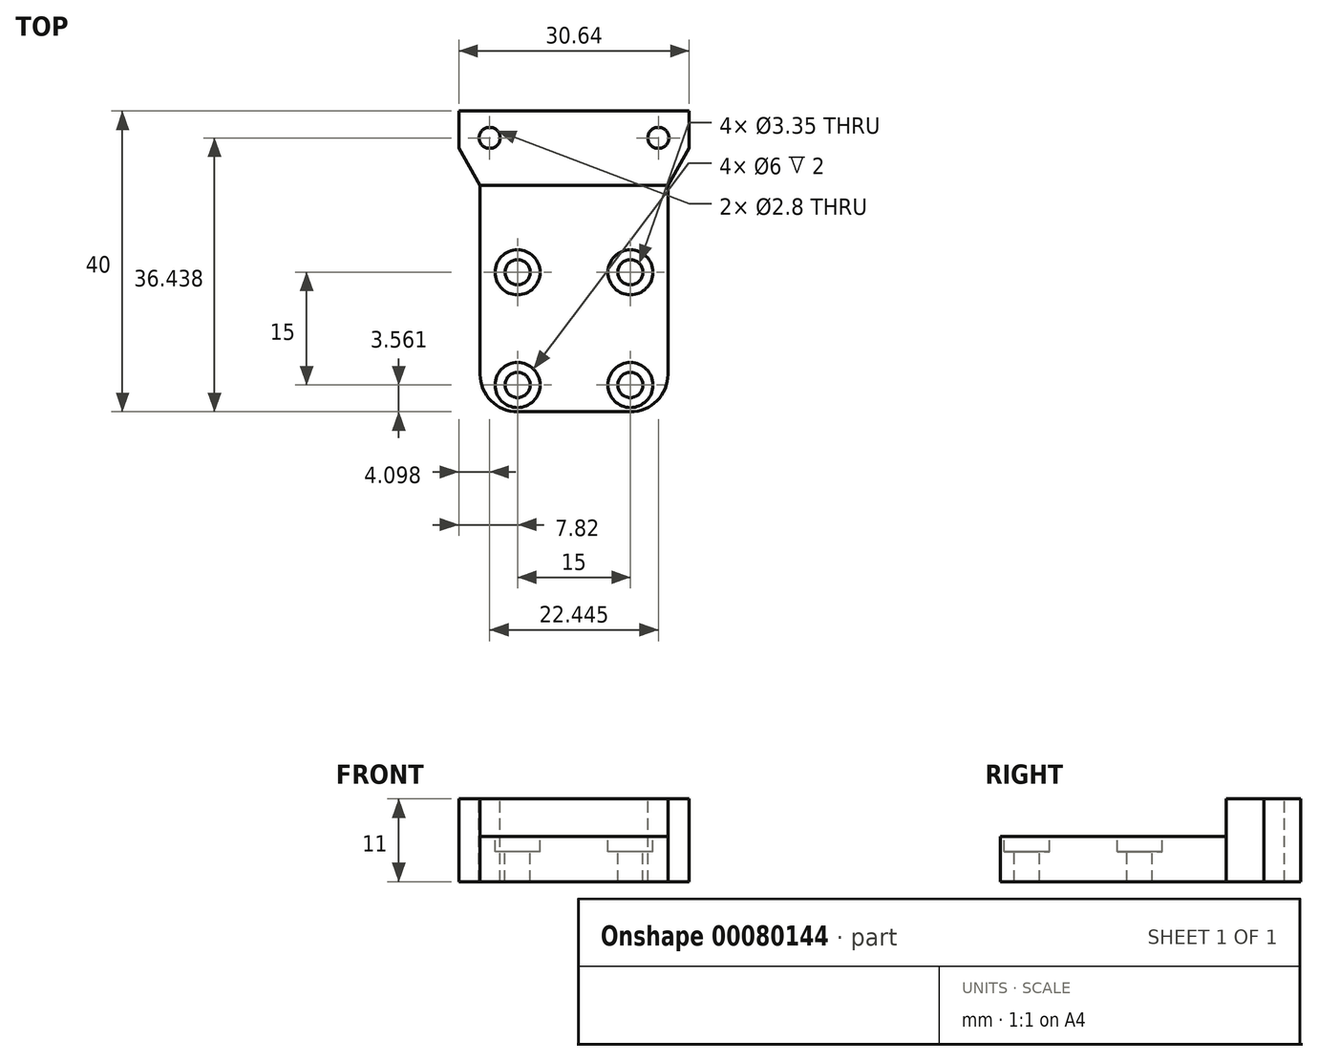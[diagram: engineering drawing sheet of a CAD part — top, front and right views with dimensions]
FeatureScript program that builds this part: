
annotation { "Feature Type Name" : "Feature", "Feature Type Description" : "" }
export const myFeature = defineFeature(function(context is Context, id is Id, definition is map)
    precondition{}
    {
        {
            var Q0;
            Q0=qCreatedBy(makeId("Top.planeOp"),FACE);
            var sketch = newSketch(context, id + "F0", { "sketchPlane" : qUnion([Q0])});
            skLineSegment(sketch, "E0.bottom", {"start": v(0, 0) * mm, "end": v(25, 0) * mm});
            skLineSegment(sketch, "E0.top", {"start": v(-2.82, 40) * mm, "end": v(27.82, 40) * mm});
            skLineSegment(sketch, "E1", {"start": v(0, 30.1) * mm, "end": v(25, 30.1) * mm});
            skLineSegment(sketch, "E2", {"start": v(-2.82, 35.1) * mm, "end": v(27.82, 35.1) * mm});
            skLineSegment(sketch, "E3", {"start": v(0, 0) * mm, "end": v(0, 30.1) * mm});
            skLineSegment(sketch, "E4", {"start": v(0, 30.1) * mm, "end": v(-2.82, 35.1) * mm});
            skLineSegment(sketch, "E5", {"start": v(-2.82, 35.1) * mm, "end": v(-2.82, 40) * mm});
            skLineSegment(sketch, "E6", {"start": v(25, 0) * mm, "end": v(25, 30.1) * mm});
            skLineSegment(sketch, "E7", {"start": v(25, 30.1) * mm, "end": v(27.82, 35.1) * mm});
            skLineSegment(sketch, "E8", {"start": v(27.82, 35.1) * mm, "end": v(27.82, 40) * mm});
            skSolve(sketch);
        }
        {
            var Q0;
            Q0=qSketchRegion(id+"F0",true);
            extrude(context, id + "F1", {"entities" : qUnion([Q0]), "depth" : 6 * mm});
        }
        {
            var Q0;
            Q0=makeQuery(id+"F1.opExtrude","CAP_FACE",FACE,{"disambiguationData":[OSD([sQuery(id+"F0.wireOp",EDGE,"E0.bottom"),sQuery(id+"F0.wireOp",EDGE,"E0.top"),sQuery(id+"F0.wireOp",EDGE,"E3"),sQuery(id+"F0.wireOp",EDGE,"E4"),sQuery(id+"F0.wireOp",EDGE,"E5"),sQuery(id+"F0.wireOp",EDGE,"E6"),sQuery(id+"F0.wireOp",EDGE,"E7"),sQuery(id+"F0.wireOp",EDGE,"E8")])],"isStart":false});
            var sketch = newSketch(context, id + "F2", { "sketchPlane" : qUnion([Q0])});
            skCircle(sketch, "E9", {"center": v(5, 18.56) * mm, "radius": 1.68 * mm});
            skCircle(sketch, "E10", {"center": v(20, 18.56) * mm, "radius": 1.68 * mm});
            skCircle(sketch, "E11", {"center": v(5, 3.56) * mm, "radius": 1.68 * mm});
            skCircle(sketch, "E12", {"center": v(20, 3.56) * mm, "radius": 1.68 * mm});
            skLineSegment(sketch, "E13", {"start": v(5, 18.56) * mm, "end": v(0, 18.56) * mm});
            skLineSegment(sketch, "E14", {"start": v(20, 3.56) * mm, "end": v(25, 3.56) * mm});
            skCircle(sketch, "E15", {"center": v(5, 18.56) * mm, "radius": 3 * mm});
            skCircle(sketch, "E16", {"center": v(20, 18.56) * mm, "radius": 3 * mm});
            skCircle(sketch, "E17", {"center": v(5, 3.56) * mm, "radius": 3 * mm});
            skCircle(sketch, "E18", {"center": v(20, 3.56) * mm, "radius": 3 * mm});
            skSolve(sketch);
        }
        {
            var Q0;
            Q0=makeQuery(id+"F2.imprint","IMPRINT",FACE,{"disambiguationData":[TD([[makeQuery(id+"F2.imprint","IMPRINT",EDGE,{"derivedFrom":sQuery(id+"F2.wireOp",EDGE,"E9")}),1.0]])]});
            var Q1;
            Q1=makeQuery(id+"F2.imprint","IMPRINT",FACE,{"disambiguationData":[TD([[makeQuery(id+"F2.imprint","IMPRINT",EDGE,{"derivedFrom":sQuery(id+"F2.wireOp",EDGE,"E10")}),1.0]])]});
            var Q2;
            Q2=makeQuery(id+"F2.imprint","IMPRINT",FACE,{"disambiguationData":[TD([[makeQuery(id+"F2.imprint","IMPRINT",EDGE,{"derivedFrom":sQuery(id+"F2.wireOp",EDGE,"E12")}),1.0]])]});
            var Q3;
            Q3=makeQuery(id+"F2.imprint","IMPRINT",FACE,{"disambiguationData":[TD([[makeQuery(id+"F2.imprint","IMPRINT",EDGE,{"derivedFrom":sQuery(id+"F2.wireOp",EDGE,"E11")}),1.0]])]});
            var Q4;
            Q4=makeQuery(id+"F2.imprint","IMPRINT",FACE,{"disambiguationData":[TD([[makeQuery(id+"F2.imprint","IMPRINT",EDGE,{"derivedFrom":sQuery(id+"F2.wireOp",EDGE,"97d24b09-4827-4c46-a1fd-a3ea8677536d")}),1.0]])]});
            var Q5;
            Q5=makeQuery(id+"F2.imprint","IMPRINT",FACE,{"disambiguationData":[TD([[makeQuery(id+"F2.imprint","IMPRINT",EDGE,{"derivedFrom":sQuery(id+"F2.wireOp",EDGE,"b6eb7b6f-8bb0-4363-9520-a6d7085f5256")}),1.0]])]});
            extrude(context, id + "F3", {"entities" : qUnion([Q0, Q1, Q2, Q3, Q4, Q5]), "operationType" : NewBodyOperationType.REMOVE, "oppositeDirection" : true, "depth" : 25 * mm});
        }
        {
            var Q0;
            Q0=makeQuery(id+"F2.imprint","IMPRINT",FACE,{"disambiguationData":[TD([[makeQuery(id+"F2.imprint","IMPRINT",EDGE,{"derivedFrom":sQuery(id+"F2.wireOp",EDGE,"E9")}),-1.0]])]});
            var Q1;
            Q1=makeQuery(id+"F2.imprint","IMPRINT",FACE,{"disambiguationData":[TD([[makeQuery(id+"F2.imprint","IMPRINT",EDGE,{"derivedFrom":sQuery(id+"F2.wireOp",EDGE,"E10")}),-1.0]])]});
            var Q2;
            Q2=makeQuery(id+"F2.imprint","IMPRINT",FACE,{"disambiguationData":[TD([[makeQuery(id+"F2.imprint","IMPRINT",EDGE,{"derivedFrom":sQuery(id+"F2.wireOp",EDGE,"E12")}),-1.0]])]});
            var Q3;
            Q3=makeQuery(id+"F2.imprint","IMPRINT",FACE,{"disambiguationData":[TD([[makeQuery(id+"F2.imprint","IMPRINT",EDGE,{"derivedFrom":sQuery(id+"F2.wireOp",EDGE,"E11")}),-1.0]])]});
            extrude(context, id + "F4", {"entities" : qUnion([Q0, Q1, Q2, Q3]), "operationType" : NewBodyOperationType.REMOVE, "oppositeDirection" : true, "depth" : 2 * mm});
        }
        {
            var Q0;
            Q0=makeQuery(id+"F1.opExtrude","SWEPT_EDGE",EDGE,{"disambiguationData":[OSD([sQuery(id+"F0.wireOp",EDGE,"E0.bottom"),sQuery(id+"F0.wireOp",EDGE,"E0.left")])]});
            var Q1;
            Q1=makeQuery(id+"F1.opExtrude","SWEPT_EDGE",EDGE,{"disambiguationData":[OSD([sQuery(id+"F0.wireOp",EDGE,"E0.bottom"),sQuery(id+"F0.wireOp",EDGE,"E0.right")])]});
            fillet(context, id + "F5", {"entities" : qUnion([Q0, Q1]), "radius" : 5 * mm, "tangentPropagation" : true, "allowEdgeOverflow" : false});
        }
        {
            var Q0;
            Q0=makeQuery(id+"F0.imprint","IMPRINT",FACE,{"disambiguationData":[TD([[makeQuery(id+"F0.imprint","IMPRINT",EDGE,{"derivedFrom":sQuery(id+"F0.wireOp",EDGE,"E0.top")}),-1.0]])]});
            var Q1;
            Q1=makeQuery(id+"F0.imprint","IMPRINT",FACE,{"disambiguationData":[TD([[makeQuery(id+"F0.imprint","IMPRINT",EDGE,{"derivedFrom":sQuery(id+"F0.wireOp",EDGE,"E1")}),1.0]])]});
            extrude(context, id + "F6", {"entities" : qUnion([Q0, Q1]), "operationType" : NewBodyOperationType.ADD, "depth" : 11 * mm});
        }
        {
            var Q0;
            Q0=makeQuery(id+"F6.opExtrude","CAP_FACE",FACE,{"disambiguationData":[OSD([sQuery(id+"F0.wireOp",EDGE,"E0.top"),sQuery(id+"F0.wireOp",EDGE,"E1"),sQuery(id+"F0.wireOp",EDGE,"E4"),sQuery(id+"F0.wireOp",EDGE,"E5"),sQuery(id+"F0.wireOp",EDGE,"E7"),sQuery(id+"F0.wireOp",EDGE,"E8")])],"isStart":false});
            var sketch = newSketch(context, id + "F7", { "sketchPlane" : qUnion([Q0])});
            skCircle(sketch, "E19", {"center": v(23.72, 36.44) * mm, "radius": 1.4 * mm});
            skCircle(sketch, "E20", {"center": v(1.28, 36.44) * mm, "radius": 1.4 * mm});
            skLineSegment(sketch, "E21", {"start": v(1.28, 36.44) * mm, "end": v(-2.82, 36.44) * mm});
            skLineSegment(sketch, "E22", {"start": v(23.72, 36.44) * mm, "end": v(27.82, 36.44) * mm});
            skSolve(sketch);
        }
        {
            var Q0;
            Q0=qSketchRegion(id+"F7",true);
            extrude(context, id + "F8", {"entities" : qUnion([Q0]), "operationType" : NewBodyOperationType.REMOVE, "endBound" : BoundingType.THROUGH_ALL, "oppositeDirection" : true, "depth" : 25 * mm});
        }
    });
